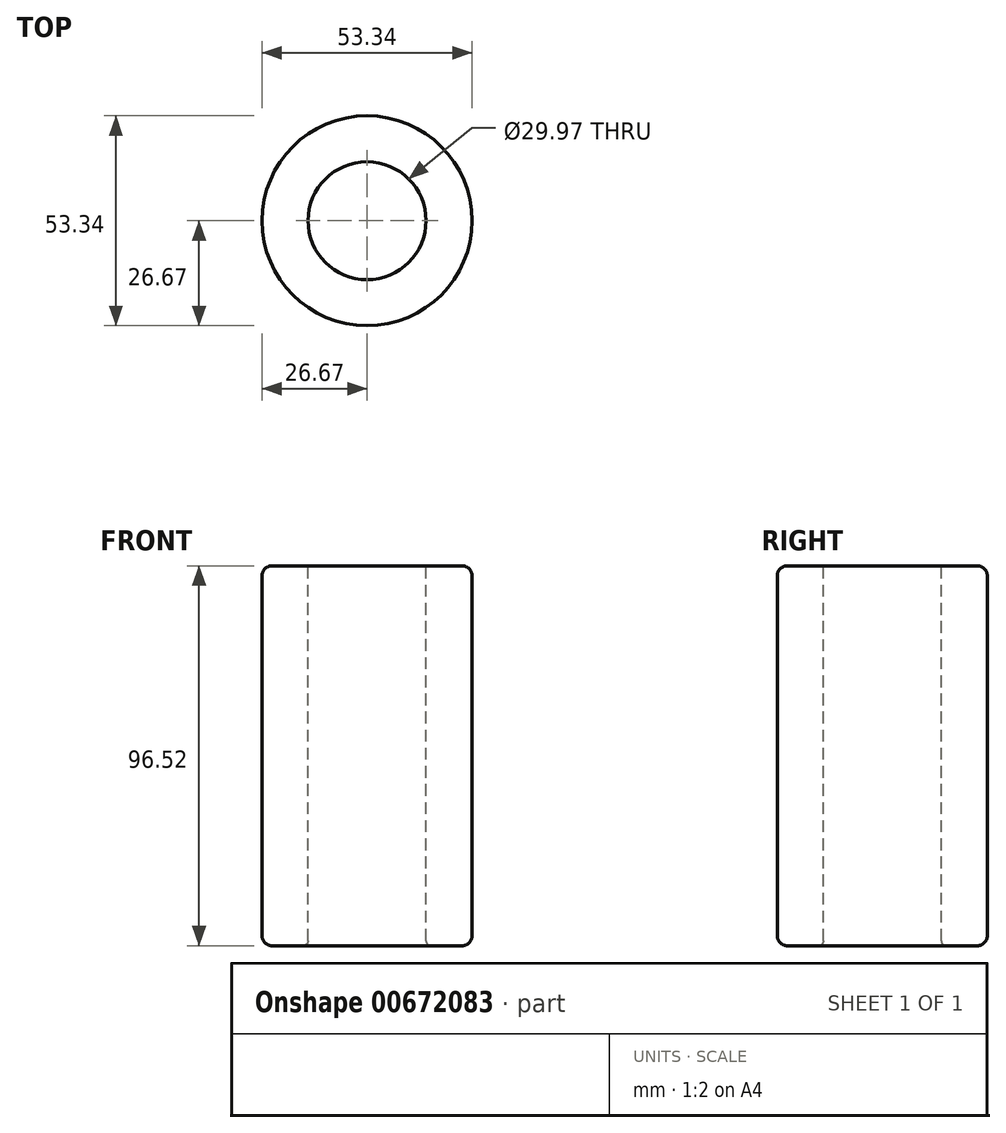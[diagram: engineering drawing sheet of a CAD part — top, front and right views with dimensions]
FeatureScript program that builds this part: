
annotation { "Feature Type Name" : "Feature", "Feature Type Description" : "" }
export const myFeature = defineFeature(function(context is Context, id is Id, definition is map)
    precondition{}
    {
        {
            var Q0;
            Q0=qCreatedBy(makeId("Top.planeOp"),FACE);
            var sketch = newSketch(context, id + "F0", { "sketchPlane" : qUnion([Q0])});
            skCircle(sketch, "E0", {"center": v(0, 0) * mm, "radius": 26.67 * mm});
            skSolve(sketch);
        }
        {
            var Q0;
            Q0 = qSketchRegion(id + "F0", true);
            extrude(context, id + "F1", {"entities" : qUnion([Q0]), "depth" : 96.52 * mm, "offsetDistance" : 25.4 * mm});
        }
        {
            var Q0;
            Q0=makeQuery(id+"F1.opExtrude","CAP_FACE",FACE,{"disambiguationData":[OSD([sQuery(id+"F0.wireOp",EDGE,"E0")])],"isStart":false});
            var sketch = newSketch(context, id + "F2", { "sketchPlane" : qUnion([Q0])});
            skCircle(sketch, "E1", {"center": v(0, 0) * mm, "radius": 14.99 * mm});
            skSolve(sketch);
        }
        {
            var Q0;
            Q0 = qSketchRegion(id + "F2", true);
            extrude(context, id + "F3", {"entities" : qUnion([Q0]), "operationType" : NewBodyOperationType.REMOVE, "endBound" : BoundingType.THROUGH_ALL, "oppositeDirection" : true, "depth" : 25.4 * mm, "offsetDistance" : 25.4 * mm});
        }
        {
            var Q0;
            Q0=makeQuery(id+"F1.opExtrude","CAP_EDGE",EDGE,{"disambiguationData":[OSD([sQuery(id+"F0.wireOp",EDGE,"E0")])],"isStart":true});
            var Q1;
            Q1=makeQuery(id+"F1.opExtrude","CAP_EDGE",EDGE,{"disambiguationData":[OSD([sQuery(id+"F0.wireOp",EDGE,"E0")])],"isStart":false});
            fillet(context, id + "F4", {"entities" : qUnion([Q0, Q1]), "radius" : 2.54 * mm, "tangentPropagation" : true, "allowEdgeOverflow" : false});
        }
        {
            var Q0;
            Q0=makeQuery(id+"F3.boolean.opBoolean","COPY",EDGE,{"derivedFrom":makeQuery(id+"F3.opExtrude","CAP_EDGE",EDGE,{"disambiguationData":[OSD([sQuery(id+"F2.wireOp",EDGE,"E1")])],"isStart":true})});
            var Q1;
            Q1=makeQuery(id+"F3.boolean.opBoolean","INTERSECT",EDGE,{"derivedFrom":[makeQuery(id+"F1.opExtrude","CAP_FACE",FACE,{"disambiguationData":[OSD([sQuery(id+"F0.wireOp",EDGE,"E0")])],"isStart":true}),makeQuery(id+"F3.opExtrude","SWEPT_FACE",FACE,{"disambiguationData":[OSD([sQuery(id+"F2.wireOp",EDGE,"E1")])]})]});
            fillet(context, id + "F5", {"entities" : qUnion([Q0, Q1]), "radius" : 1.27 * mm, "tangentPropagation" : true, "allowEdgeOverflow" : false});
        }
    });
